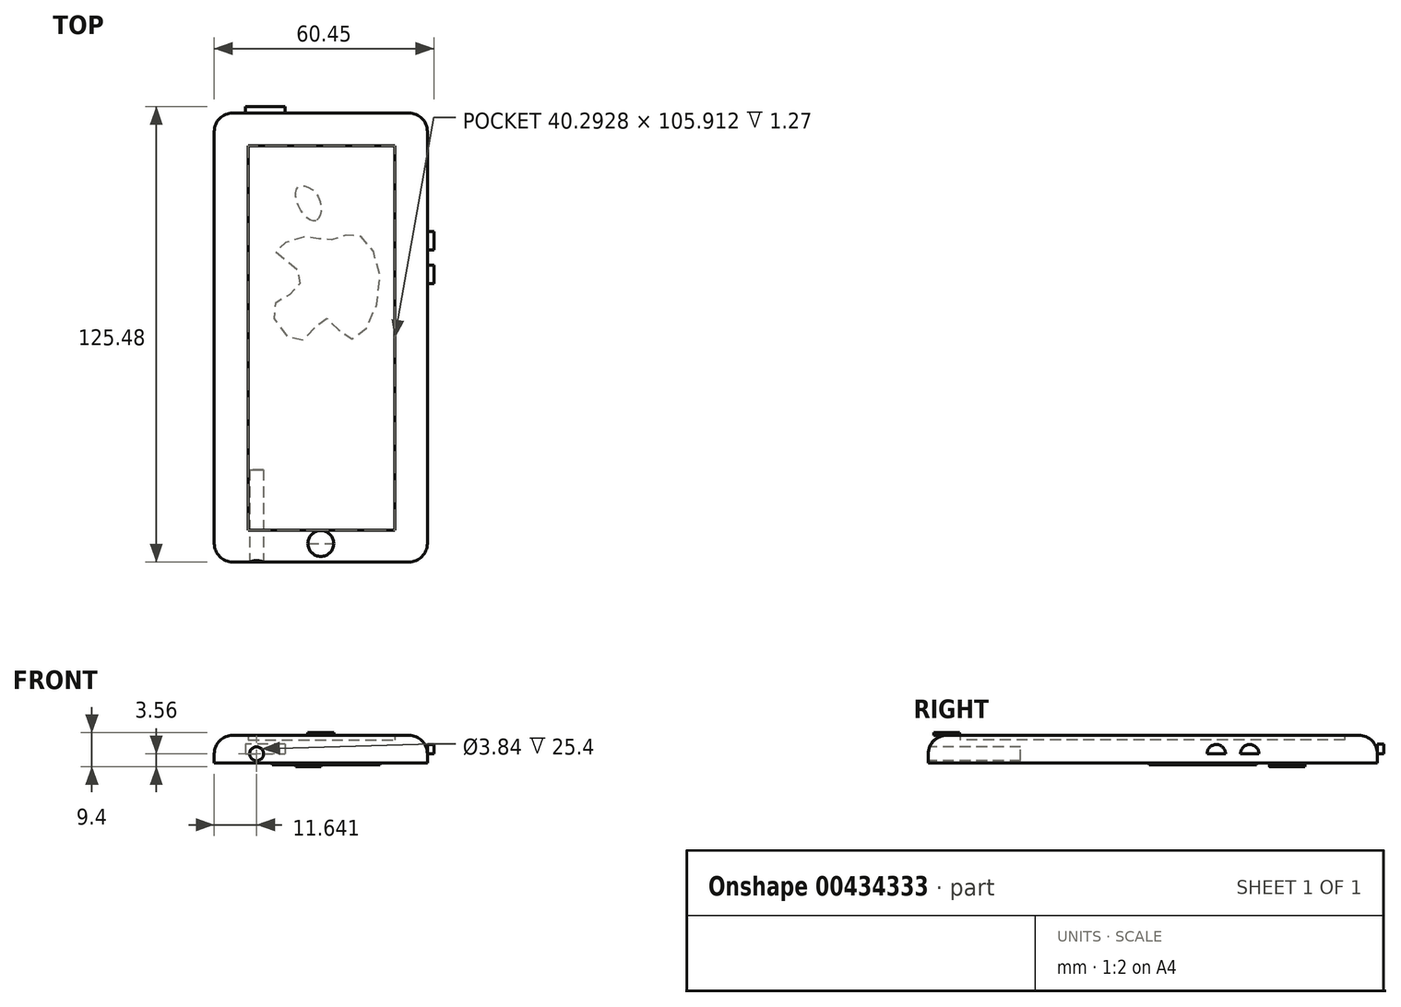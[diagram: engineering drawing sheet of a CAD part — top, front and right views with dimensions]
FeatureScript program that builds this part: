
annotation { "Feature Type Name" : "Feature", "Feature Type Description" : "" }
export const myFeature = defineFeature(function(context is Context, id is Id, definition is map)
    precondition{}
    {
        {
            var Q0;
            Q0=qCreatedBy(makeId("Top.planeOp"),FACE);
            var sketch = newSketch(context, id + "F0", { "sketchPlane" : qUnion([Q0])});
            skLineSegment(sketch, "E0.bottom", {"start": v(-64.35, 70.89) * mm, "end": v(-5.68, 70.89) * mm});
            skLineSegment(sketch, "E0.top", {"start": v(-64.35, -52.8) * mm, "end": v(-5.68, -52.8) * mm});
            skLineSegment(sketch, "E0.left", {"start": v(-64.35, 70.89) * mm, "end": v(-64.35, -52.8) * mm});
            skLineSegment(sketch, "E0.right", {"start": v(-5.68, 70.89) * mm, "end": v(-5.68, -52.8) * mm});
            skSolve(sketch);
        }
        {
            var Q0;
            Q0=makeQuery(id+"F0.imprint","IMPRINT",FACE,{"disambiguationData":[TD([[makeQuery(id+"F0.imprint","IMPRINT",EDGE,{"derivedFrom":sQuery(id+"F0.wireOp",EDGE,"E0.bottom")}),-1.0]])]});
            extrude(context, id + "F1", {"entities" : qUnion([Q0]), "depth" : 7.62 * mm});
        }
        {
            var Q0;
            Q0=makeQuery(id+"F1.opExtrude","CAP_EDGE",EDGE,{"disambiguationData":[OSD([sQuery(id+"F0.wireOp",EDGE,"E0.left")])],"isStart":false});
            fillet(context, id + "F2", {"entities" : qUnion([Q0]), "radius" : 5.08 * mm, "tangentPropagation" : true, "allowEdgeOverflow" : false});
        }
        {
            var Q0;
            Q0=makeQuery(id+"F1.opExtrude","CAP_EDGE",EDGE,{"disambiguationData":[OSD([sQuery(id+"F0.wireOp",EDGE,"E0.bottom")])],"isStart":false});
            fillet(context, id + "F3", {"entities" : qUnion([Q0]), "radius" : 5.08 * mm, "tangentPropagation" : true, "allowEdgeOverflow" : false});
        }
        {
            var Q0;
            Q0=makeQuery(id+"F1.opExtrude","CAP_EDGE",EDGE,{"disambiguationData":[OSD([sQuery(id+"F0.wireOp",EDGE,"E0.right")])],"isStart":false});
            fillet(context, id + "F4", {"entities" : qUnion([Q0]), "radius" : 5.08 * mm, "tangentPropagation" : true, "allowEdgeOverflow" : false});
        }
        {
            var Q0;
            Q0=makeQuery(id+"F1.opExtrude","CAP_EDGE",EDGE,{"disambiguationData":[OSD([sQuery(id+"F0.wireOp",EDGE,"E0.top")])],"isStart":false});
            fillet(context, id + "F5", {"entities" : qUnion([Q0]), "radius" : 5.08 * mm, "tangentPropagation" : true, "allowEdgeOverflow" : false});
        }
        {
            var Q0;
            Q0=makeQuery(id+"F1.opExtrude","CAP_FACE",FACE,{"disambiguationData":[OSD([sQuery(id+"F0.wireOp",EDGE,"E0.bottom"),sQuery(id+"F0.wireOp",EDGE,"E0.top"),sQuery(id+"F0.wireOp",EDGE,"E0.left"),sQuery(id+"F0.wireOp",EDGE,"E0.right")])],"isStart":false});
            var sketch = newSketch(context, id + "F6", { "sketchPlane" : qUnion([Q0])});
            skLineSegment(sketch, "E1.bottom", {"start": v(-54.97, 61.88) * mm, "end": v(-14.68, 61.88) * mm});
            skLineSegment(sketch, "E1.top", {"start": v(-54.97, -44.03) * mm, "end": v(-14.68, -44.03) * mm});
            skLineSegment(sketch, "E1.left", {"start": v(-54.97, 61.88) * mm, "end": v(-54.97, -44.03) * mm});
            skLineSegment(sketch, "E1.right", {"start": v(-14.68, 61.88) * mm, "end": v(-14.68, -44.03) * mm});
            skSolve(sketch);
        }
        {
            var Q0;
            Q0=makeQuery(id+"F6.imprint","IMPRINT",FACE,{"disambiguationData":[TD([[makeQuery(id+"F6.imprint","IMPRINT",EDGE,{"derivedFrom":sQuery(id+"F6.wireOp",EDGE,"E1.bottom")}),-1.0]])]});
            extrude(context, id + "F7", {"entities" : qUnion([Q0]), "operationType" : NewBodyOperationType.REMOVE, "oppositeDirection" : true, "depth" : 1.27 * mm});
        }
        {
            var Q0;
            Q0=makeQuery(id+"F7.boolean.opBoolean","COPY",FACE,{"derivedFrom":makeQuery(id+"F7.opExtrude","CAP_FACE",FACE,{"disambiguationData":[OSD([sQuery(id+"F6.wireOp",EDGE,"E1.bottom"),sQuery(id+"F6.wireOp",EDGE,"E1.top"),sQuery(id+"F6.wireOp",EDGE,"E1.left"),sQuery(id+"F6.wireOp",EDGE,"E1.right")])],"isStart":false})});
            var sketch = newSketch(context, id + "F8", { "sketchPlane" : qUnion([Q0])});
            skLineSegment(sketch, "E2.bottom", {"start": v(-54.97, 61.88) * mm, "end": v(-14.68, 61.88) * mm});
            skLineSegment(sketch, "E2.top", {"start": v(-54.97, -44.03) * mm, "end": v(-14.68, -44.03) * mm});
            skLineSegment(sketch, "E2.left", {"start": v(-54.97, 61.88) * mm, "end": v(-54.97, -44.03) * mm});
            skLineSegment(sketch, "E2.right", {"start": v(-14.68, 61.88) * mm, "end": v(-14.68, -44.03) * mm});
            skSolve(sketch);
        }
        {
            var Q0;
            Q0=makeQuery(id+"F8.imprint","IMPRINT",FACE,{"disambiguationData":[TD([[makeQuery(id+"F8.imprint","IMPRINT",EDGE,{"derivedFrom":sQuery(id+"F8.wireOp",EDGE,"E2.bottom")}),-1.0]])]});
            extrude(context, id + "F9", {"entities" : qUnion([Q0]), "depth" : 1.27 * mm});
        }
        {
            var Q0;
            Q0=makeQuery(id+"F1.opExtrude","SWEPT_FACE",FACE,{"disambiguationData":[OSD([sQuery(id+"F0.wireOp",EDGE,"E0.right")])]});
            var sketch = newSketch(context, id + "F10", { "sketchPlane" : qUnion([Q0])});
            skCircle(sketch, "E3", {"center": v(35.69, 2.54) * mm, "radius": 2.54 * mm});
            skSolve(sketch);
        }
        {
            var Q0;
            Q0=makeQuery(id+"F1.opExtrude","SWEPT_FACE",FACE,{"disambiguationData":[OSD([sQuery(id+"F0.wireOp",EDGE,"E0.right")])]});
            var sketch = newSketch(context, id + "F11", { "sketchPlane" : qUnion([Q0])});
            skCircle(sketch, "E4", {"center": v(26.48, 2.54) * mm, "radius": 2.54 * mm});
            skSolve(sketch);
        }
        {
            var Q0;
            Q0=makeQuery(id+"F1.opExtrude","SWEPT_FACE",FACE,{"disambiguationData":[OSD([sQuery(id+"F0.wireOp",EDGE,"E0.bottom")])]});
            var sketch = newSketch(context, id + "F12", { "sketchPlane" : qUnion([Q0])});
            skLineSegment(sketch, "E5.bottom", {"start": v(44.9, 5.18) * mm, "end": v(55.83, 5.18) * mm});
            skLineSegment(sketch, "E5.top", {"start": v(44.9, 2.54) * mm, "end": v(55.83, 2.54) * mm});
            skLineSegment(sketch, "E5.left", {"start": v(44.9, 5.18) * mm, "end": v(44.9, 2.54) * mm});
            skLineSegment(sketch, "E5.right", {"start": v(55.83, 5.18) * mm, "end": v(55.83, 2.54) * mm});
            skSolve(sketch);
        }
        {
            var Q0;
            {var subQ0=sQuery(id+"F11.wireOp",EDGE,"E4");var subQ1=sQuery(id+"F0.wireOp",EDGE,"E0.right");var subQ2=makeQuery(id+"F4.opFillet","BLEND_EDGE",EDGE,{"blendedFrom":[makeQuery(id+"F1.opExtrude","CAP_EDGE",EDGE,{"disambiguationData":[OSD([subQ1])],"isStart":false}),makeQuery(id+"F1.opExtrude","SWEPT_FACE",FACE,{"disambiguationData":[OSD([subQ1])]})],"blendedInto":[makeQuery(id+"F1.opExtrude","SWEPT_FACE",FACE,{"disambiguationData":[OSD([subQ1])]})]});var subQ3=makeQuery(id+"F11.imprint","INTERSECT",VERTEX,{"disambiguationData":[OD(0.0)],"derivedFrom":[subQ2,subQ0]});Q0=makeQuery(id+"F11.imprint","IMPRINT",FACE,{"disambiguationData":[TD([[makeQuery(id+"F11.imprint","IMPRINT",EDGE,{"disambiguationData":[TD([[subQ3,1.0]])],"derivedFrom":subQ0}),1.0]])]});}
            extrude(context, id + "F13", {"entities" : qUnion([Q0]), "depth" : 1.78 * mm});
        }
        {
            var Q0;
            Q0=makeQuery(id+"F12.imprint","IMPRINT",FACE,{"disambiguationData":[TD([[makeQuery(id+"F12.imprint","IMPRINT",EDGE,{"derivedFrom":sQuery(id+"F12.wireOp",EDGE,"E5.bottom")}),-1.0]])]});
            extrude(context, id + "F14", {"entities" : qUnion([Q0]), "depth" : 1.78 * mm});
        }
        {
            var Q0;
            Q0=makeQuery(id+"F1.opExtrude","CAP_FACE",FACE,{"disambiguationData":[OSD([sQuery(id+"F0.wireOp",EDGE,"E0.bottom"),sQuery(id+"F0.wireOp",EDGE,"E0.top"),sQuery(id+"F0.wireOp",EDGE,"E0.left"),sQuery(id+"F0.wireOp",EDGE,"E0.right")])],"isStart":false});
            var sketch = newSketch(context, id + "F15", { "sketchPlane" : qUnion([Q0])});
            skCircle(sketch, "E6", {"center": v(-35.02, -47.73) * mm, "radius": 3.56 * mm});
            skSolve(sketch);
        }
        {
            var Q0;
            {var subQ0=sQuery(id+"F10.wireOp",EDGE,"E3");var subQ1=sQuery(id+"F0.wireOp",EDGE,"E0.right");var subQ2=makeQuery(id+"F4.opFillet","BLEND_EDGE",EDGE,{"blendedFrom":[makeQuery(id+"F1.opExtrude","CAP_EDGE",EDGE,{"disambiguationData":[OSD([subQ1])],"isStart":false}),makeQuery(id+"F1.opExtrude","SWEPT_FACE",FACE,{"disambiguationData":[OSD([subQ1])]})],"blendedInto":[makeQuery(id+"F1.opExtrude","SWEPT_FACE",FACE,{"disambiguationData":[OSD([subQ1])]})]});var subQ3=makeQuery(id+"F10.imprint","INTERSECT",VERTEX,{"disambiguationData":[OD(0.0)],"derivedFrom":[subQ2,subQ0]});Q0=makeQuery(id+"F10.imprint","IMPRINT",FACE,{"disambiguationData":[TD([[makeQuery(id+"F10.imprint","IMPRINT",EDGE,{"disambiguationData":[TD([[subQ3,1.0]])],"derivedFrom":subQ0}),1.0]])]});}
            extrude(context, id + "F16", {"entities" : qUnion([Q0]), "depth" : 1.78 * mm});
        }
        {
            var Q0;
            {var subQ0=sQuery(id+"F15.wireOp",EDGE,"E6");var subQ1=sQuery(id+"F0.wireOp",EDGE,"E0.top");var subQ2=makeQuery(id+"F5.opFillet","BLEND_EDGE",EDGE,{"blendedFrom":[makeQuery(id+"F1.opExtrude","CAP_EDGE",EDGE,{"disambiguationData":[OSD([subQ1])],"isStart":false}),makeQuery(id+"F1.opExtrude","CAP_FACE",FACE,{"disambiguationData":[OSD([sQuery(id+"F0.wireOp",EDGE,"E0.bottom"),subQ1,sQuery(id+"F0.wireOp",EDGE,"E0.left"),sQuery(id+"F0.wireOp",EDGE,"E0.right")])],"isStart":false})],"blendedInto":[makeQuery(id+"F1.opExtrude","CAP_FACE",FACE,{"disambiguationData":[OSD([sQuery(id+"F0.wireOp",EDGE,"E0.bottom"),subQ1,sQuery(id+"F0.wireOp",EDGE,"E0.left"),sQuery(id+"F0.wireOp",EDGE,"E0.right")])],"isStart":false})]});var subQ3=makeQuery(id+"F15.imprint","INTERSECT",VERTEX,{"disambiguationData":[OD(0.0)],"derivedFrom":[subQ2,subQ0]});Q0=makeQuery(id+"F15.imprint","IMPRINT",FACE,{"disambiguationData":[TD([[makeQuery(id+"F15.imprint","IMPRINT",EDGE,{"disambiguationData":[TD([[subQ3,1.0]])],"derivedFrom":subQ0}),1.0]])]});}
            var Q1;
            {var subQ0=sQuery(id+"F15.wireOp",EDGE,"E6");var subQ1=sQuery(id+"F0.wireOp",EDGE,"E0.top");var subQ2=makeQuery(id+"F5.opFillet","BLEND_EDGE",EDGE,{"blendedFrom":[makeQuery(id+"F1.opExtrude","CAP_EDGE",EDGE,{"disambiguationData":[OSD([subQ1])],"isStart":false}),makeQuery(id+"F1.opExtrude","CAP_FACE",FACE,{"disambiguationData":[OSD([sQuery(id+"F0.wireOp",EDGE,"E0.bottom"),subQ1,sQuery(id+"F0.wireOp",EDGE,"E0.left"),sQuery(id+"F0.wireOp",EDGE,"E0.right")])],"isStart":false})],"blendedInto":[makeQuery(id+"F1.opExtrude","CAP_FACE",FACE,{"disambiguationData":[OSD([sQuery(id+"F0.wireOp",EDGE,"E0.bottom"),subQ1,sQuery(id+"F0.wireOp",EDGE,"E0.left"),sQuery(id+"F0.wireOp",EDGE,"E0.right")])],"isStart":false})]});var subQ3=makeQuery(id+"F15.imprint","INTERSECT",VERTEX,{"disambiguationData":[OD(0.0)],"derivedFrom":[subQ2,subQ0]});Q1=makeQuery(id+"F15.imprint","IMPRINT",FACE,{"disambiguationData":[TD([[makeQuery(id+"F15.imprint","IMPRINT",EDGE,{"disambiguationData":[TD([[subQ3,-1.0]])],"derivedFrom":subQ0}),1.0]])]});}
            extrude(context, id + "F17", {"entities" : qUnion([Q0, Q1]), "operationType" : NewBodyOperationType.ADD, "depth" : 0.76 * mm});
        }
        {
            var Q0;
            Q0=makeQuery(id+"F1.opExtrude","CAP_FACE",FACE,{"disambiguationData":[OSD([sQuery(id+"F0.wireOp",EDGE,"E0.bottom"),sQuery(id+"F0.wireOp",EDGE,"E0.top"),sQuery(id+"F0.wireOp",EDGE,"E0.left"),sQuery(id+"F0.wireOp",EDGE,"E0.right")])],"isStart":true});
            var sketch = newSketch(context, id + "F18", { "sketchPlane" : qUnion([Q0])});
            skFitSpline(sketch, "E7", {"points": [v(-47.4, -32.67) * mm, v(-42.04, -28.56) * mm, v(-41.72, -22.25) * mm, v(-48.35, -16.89) * mm, v(-40.77, -8.05) * mm, v(-33.83, -14.36) * mm, v(-26.89, -8.68) * mm, v(-18.68, -23.51) * mm, v(-25.3, -37.4) * mm, v(-32.88, -35.82) * mm, v(-39.51, -36.77) * mm, v(-47.4, -32.67) * mm]});
            skSolve(sketch);
        }
        {
            var Q0;
            Q0=makeQuery(id+"F18.imprint","IMPRINT",FACE,{"disambiguationData":[TD([[makeQuery(id+"F18.imprint","IMPRINT",EDGE,{"derivedFrom":sQuery(id+"F18.wireOp",EDGE,"E7")}),-1.0]])]});
            extrude(context, id + "F19", {"entities" : qUnion([Q0]), "operationType" : NewBodyOperationType.ADD, "depth" : 0.5 * mm});
        }
        {
            var Q0;
            Q0=makeQuery(id+"F19.opExtrude","CAP_FACE",FACE,{"disambiguationData":[OSD([sQuery(id+"F18.wireOp",EDGE,"E7")])],"isStart":false});
            var sketch = newSketch(context, id + "F20", { "sketchPlane" : qUnion([Q0])});
            skFitSpline(sketch, "E8", {"points": [v(-36.3, -41.19) * mm, v(-41.03, -44.98) * mm, v(-41.03, -50.66) * mm, v(-35.67, -47.82) * mm, v(-36.3, -41.19) * mm]});
            skSolve(sketch);
        }
        {
            var Q0;
            Q0=makeQuery(id+"F20.imprint","IMPRINT",FACE,{"disambiguationData":[TD([[makeQuery(id+"F20.imprint","IMPRINT",EDGE,{"derivedFrom":sQuery(id+"F20.wireOp",EDGE,"E8")}),1.0]])]});
            extrude(context, id + "F21", {"entities" : qUnion([Q0]), "depth" : 0.5 * mm});
        }
        {
            var Q0;
            Q0=makeQuery(id+"F1.opExtrude","SWEPT_FACE",FACE,{"disambiguationData":[OSD([sQuery(id+"F0.wireOp",EDGE,"E0.top")])]});
            var sketch = newSketch(context, id + "F22", { "sketchPlane" : qUnion([Q0])});
            skCircle(sketch, "E9", {"center": v(-52.7, 2.54) * mm, "radius": 1.92 * mm});
            skSolve(sketch);
        }
        {
            var Q0;
            {var subQ0=sQuery(id+"F22.wireOp",EDGE,"E9");var subQ1=sQuery(id+"F0.wireOp",EDGE,"E0.top");var subQ2=makeQuery(id+"F5.opFillet","BLEND_EDGE",EDGE,{"blendedFrom":[makeQuery(id+"F1.opExtrude","CAP_EDGE",EDGE,{"disambiguationData":[OSD([subQ1])],"isStart":false}),makeQuery(id+"F1.opExtrude","SWEPT_FACE",FACE,{"disambiguationData":[OSD([subQ1])]})],"blendedInto":[makeQuery(id+"F1.opExtrude","SWEPT_FACE",FACE,{"disambiguationData":[OSD([subQ1])]})]});var subQ3=makeQuery(id+"F22.imprint","INTERSECT",VERTEX,{"disambiguationData":[OD(0.0)],"derivedFrom":[subQ2,subQ0]});Q0=makeQuery(id+"F22.imprint","IMPRINT",FACE,{"disambiguationData":[TD([[makeQuery(id+"F22.imprint","IMPRINT",EDGE,{"disambiguationData":[TD([[subQ3,1.0]])],"derivedFrom":subQ0}),1.0]])]});}
            var Q1;
            {var subQ0=sQuery(id+"F22.wireOp",EDGE,"E9");var subQ1=sQuery(id+"F0.wireOp",EDGE,"E0.top");var subQ2=makeQuery(id+"F5.opFillet","BLEND_EDGE",EDGE,{"blendedFrom":[makeQuery(id+"F1.opExtrude","CAP_EDGE",EDGE,{"disambiguationData":[OSD([subQ1])],"isStart":false}),makeQuery(id+"F1.opExtrude","SWEPT_FACE",FACE,{"disambiguationData":[OSD([subQ1])]})],"blendedInto":[makeQuery(id+"F1.opExtrude","SWEPT_FACE",FACE,{"disambiguationData":[OSD([subQ1])]})]});var subQ3=makeQuery(id+"F22.imprint","INTERSECT",VERTEX,{"disambiguationData":[OD(0.0)],"derivedFrom":[subQ2,subQ0]});Q1=makeQuery(id+"F22.imprint","IMPRINT",FACE,{"disambiguationData":[TD([[makeQuery(id+"F22.imprint","IMPRINT",EDGE,{"disambiguationData":[TD([[subQ3,-1.0]])],"derivedFrom":subQ0}),1.0]])]});}
            extrude(context, id + "F23", {"entities" : qUnion([Q0, Q1]), "operationType" : NewBodyOperationType.REMOVE, "oppositeDirection" : true, "depth" : 25.4 * mm});
        }
    });
